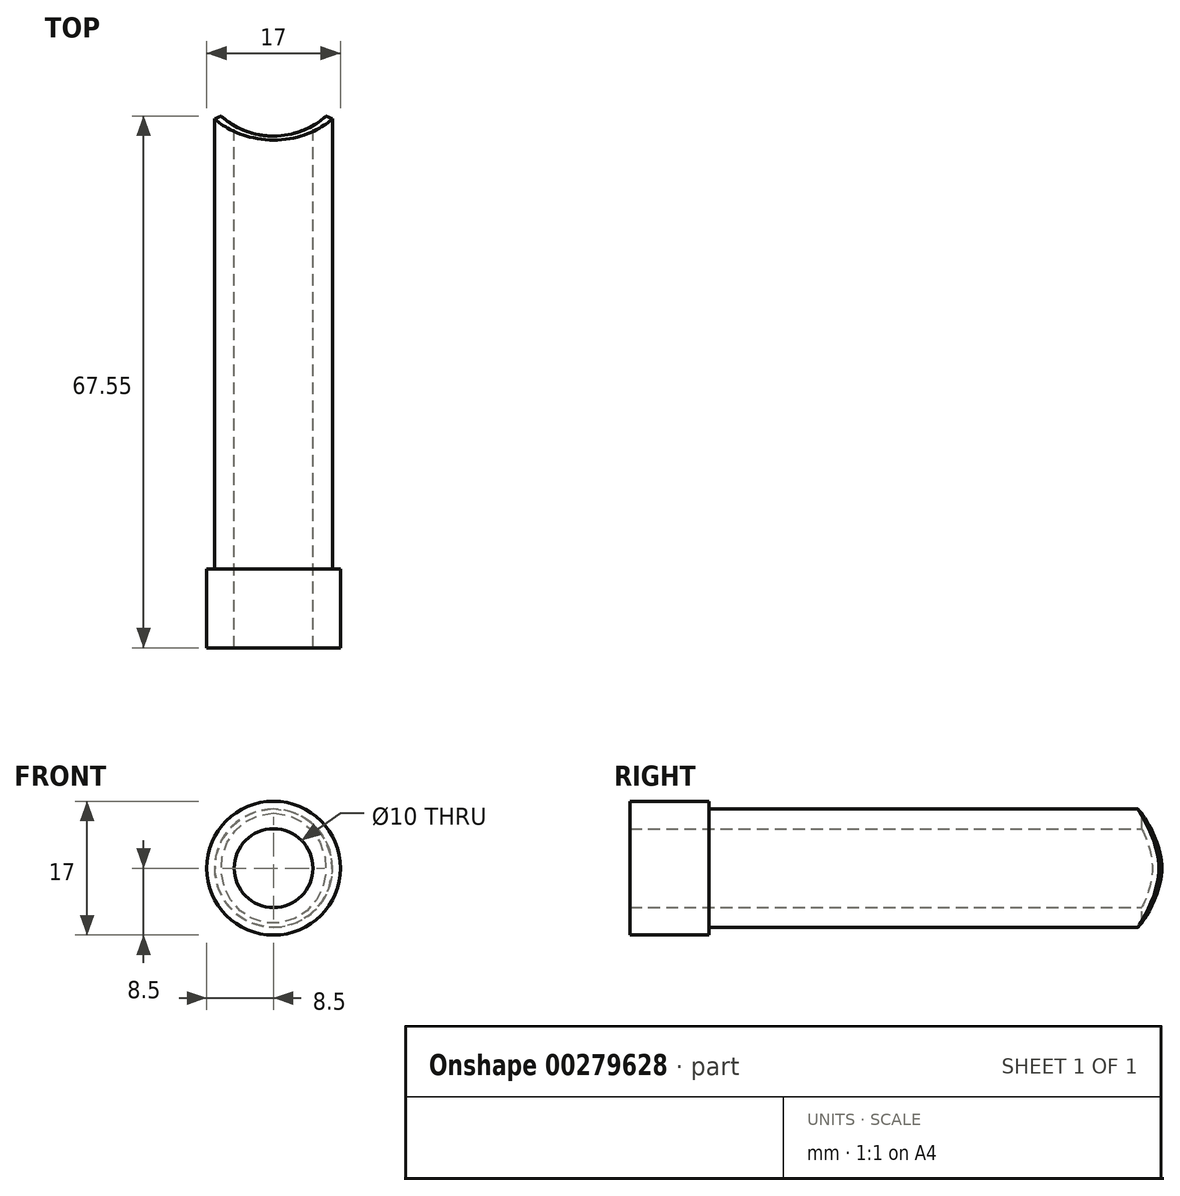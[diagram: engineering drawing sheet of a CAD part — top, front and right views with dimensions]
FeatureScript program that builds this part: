
annotation { "Feature Type Name" : "Feature", "Feature Type Description" : "" }
export const myFeature = defineFeature(function(context is Context, id is Id, definition is map)
    precondition{}
    {
        {
            var Q0;
            Q0=qCreatedBy(makeId("Front.planeOp"),FACE);
            var sketch = newSketch(context, id + "F0", { "sketchPlane" : qUnion([Q0])});
            skCircle(sketch, "E0", {"center": v(0, 0) * mm, "radius": 7.5 * mm});
            skCircle(sketch, "E1", {"center": v(0, 0) * mm, "radius": 5 * mm});
            skSolve(sketch);
        }
        {
            var Q0;
            Q0=qSketchRegion(id+"F0",true);
            extrude(context, id + "F1", {"entities" : qUnion([Q0]), "depth" : 75 * mm});
        }
        {
            var Q0;
            Q0=qCreatedBy(makeId("Right.planeOp"),FACE);
            var sketch = newSketch(context, id + "F2", { "sketchPlane" : qUnion([Q0])});
            skLineSegment(sketch, "E2", {"start": v(10, -26.26) * mm, "end": v(10, 33.54) * mm});
            skLineSegment(sketch, "E3", {"start": v(0, -31.46) * mm, "end": v(0, 43.94) * mm, "construction": true});
            skLineSegment(sketch, "E4", {"start": v(10, -26.26) * mm, "end": v(0, -26.26) * mm});
            skLineSegment(sketch, "E5", {"start": v(0, -26.26) * mm, "end": v(0, 33.54) * mm});
            skLineSegment(sketch, "E6", {"start": v(0, 33.54) * mm, "end": v(10, 33.54) * mm});
            skSolve(sketch);
        }
        {
            var Q0;
            Q0=qSketchRegion(id+"F2",true);
            var Q1;
            Q1=sQuery(id+"F2.wireOp",EDGE,"E3");
            revolve(context, id + "F3", {"operationType" : NewBodyOperationType.REMOVE, "entities" : qUnion([Q0]), "axis" : qUnion([Q1]), "revolveType" : RevolveType.FULL, "oppositeDirection" : true});
        }
        {
            var Q0;
            Q0=makeQuery(id+"F3.boolean.opBoolean","INTERSECT",EDGE,{"derivedFrom":[makeQuery(id+"F1.opExtrude","SWEPT_FACE",FACE,{"disambiguationData":[OSD([sQuery(id+"F0.wireOp",EDGE,"E0")])]}),makeQuery(id+"F3.opRevolve","SWEPT_FACE",FACE,{"disambiguationData":[OSD([sQuery(id+"F2.wireOp",EDGE,"E2")])]})]});
            chamfer(context, id + "F4", {"entities" : qUnion([Q0]), "width" : 0.5 * mm, "tangentPropagation" : true});
        }
        {
            var Q0;
            Q0=makeQuery(id+"F1.opExtrude","CAP_FACE",FACE,{"disambiguationData":[OSD([sQuery(id+"F0.wireOp",EDGE,"E0"),sQuery(id+"F0.wireOp",EDGE,"E1")])],"isStart":false});
            var sketch = newSketch(context, id + "F5", { "sketchPlane" : qUnion([Q0])});
            skCircle(sketch, "E7", {"center": v(0, 0) * mm, "radius": 8.5 * mm});
            skCircle(sketch, "E8", {"center": v(0, 0) * mm, "radius": 5 * mm});
            skSolve(sketch);
        }
        {
            var Q0;
            Q0 = qSketchRegion(id + "F5", true);
            extrude(context, id + "F6", {"entities" : qUnion([Q0]), "operationType" : NewBodyOperationType.ADD, "oppositeDirection" : true, "depth" : 10 * mm});
        }
    });
